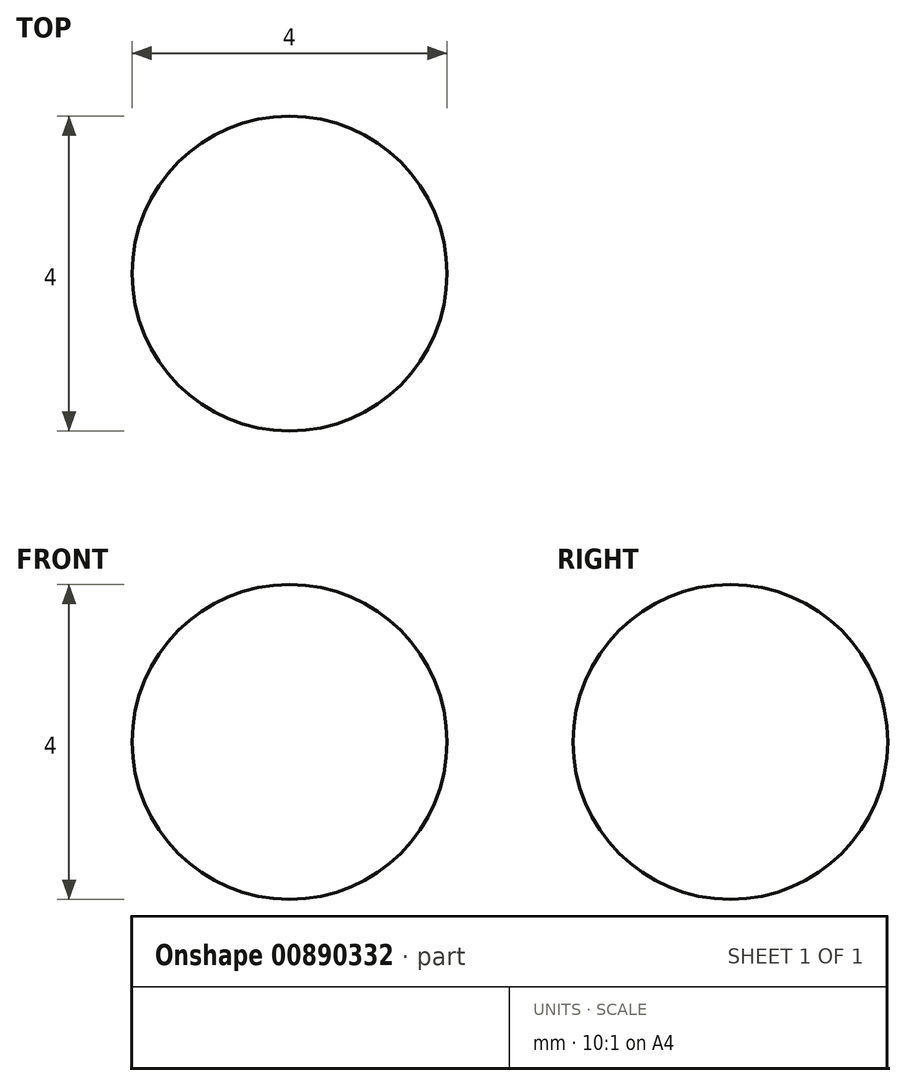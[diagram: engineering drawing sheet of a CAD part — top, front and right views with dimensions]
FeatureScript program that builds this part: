
annotation { "Feature Type Name" : "Feature", "Feature Type Description" : "" }
export const myFeature = defineFeature(function(context is Context, id is Id, definition is map)
    precondition{}
    {
        {
            var Q0;
            Q0=qCreatedBy(makeId("Top.planeOp"),FACE);
            var sketch = newSketch(context, id + "F0", { "sketchPlane" : qUnion([Q0])});
            skArc(sketch, "E0", {"start": v(2, 0) * mm, "mid": v(0, 2) * mm, "end": v(-2, 0) * mm});
            skLineSegment(sketch, "E1.trimOffspring", {"start": v(0, 0) * mm, "end": v(-8, 0) * mm, "construction": true});
            skSolve(sketch);
        }
        {
            var Q0;
            Q0 = qSketchRegion(id + "F0", true);
            var Q1;
            Q1=sQuery(id+"F0.wireOp",EDGE,"E0");
            var Q2;
            Q2=sQuery(id+"F0.wireOp",EDGE,"E1.trimOffspring");
            revolve(context, id + "F1", {"bodyType" : ToolBodyType.SURFACE, "operationType" : NewBodyOperationType.ADD, "surfaceOperationType" : NewSurfaceOperationType.NEW, "entities" : qUnion([Q0]), "surfaceEntities" : qUnion([Q1]), "axis" : qUnion([Q2]), "revolveType" : RevolveType.FULL});
        }
    });
